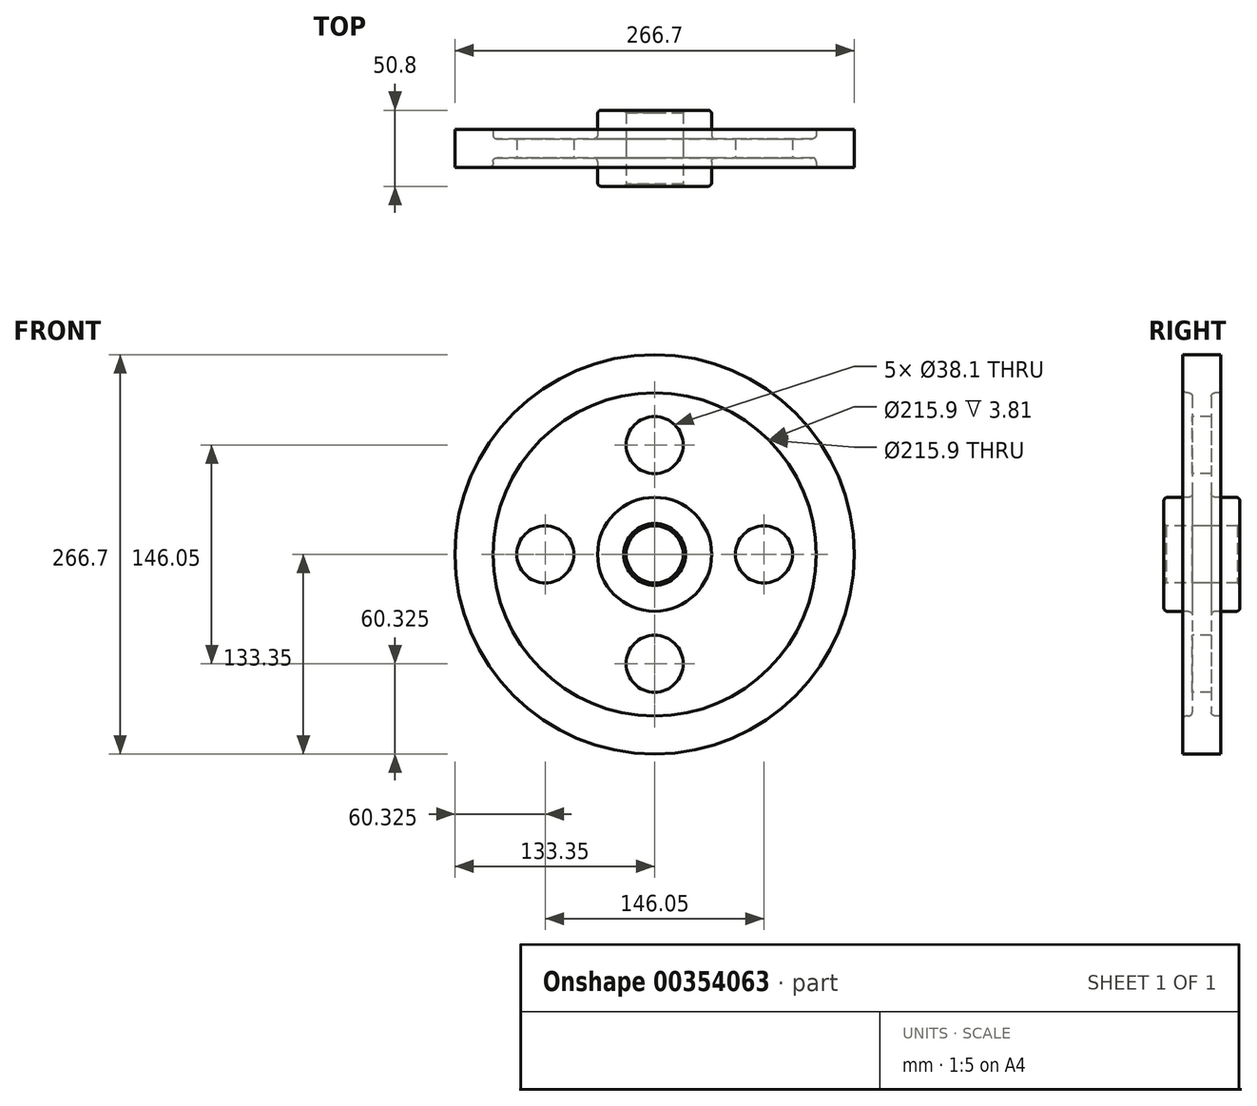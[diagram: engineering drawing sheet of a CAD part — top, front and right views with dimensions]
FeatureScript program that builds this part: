
annotation { "Feature Type Name" : "Feature", "Feature Type Description" : "" }
export const myFeature = defineFeature(function(context is Context, id is Id, definition is map)
    precondition{}
    {
        {
            var Q0;
            Q0=qCreatedBy(makeId("Right.planeOp"),FACE);
            var sketch = newSketch(context, id + "F0", { "sketchPlane" : qUnion([Q0])});
            skLineSegment(sketch, "E0", {"start": v(0, 0) * mm, "end": v(94.54, 0) * mm, "construction": true});
            skLineSegment(sketch, "E1.0", {"start": v(0, 19.05) * mm, "end": v(25.4, 19.05) * mm});
            skLineSegment(sketch, "E2.0", {"start": v(6.35, 38.1) * mm, "end": v(25.4, 38.1) * mm});
            skLineSegment(sketch, "E3.0", {"start": v(6.35, 107.95) * mm, "end": v(12.7, 107.95) * mm});
            skLineSegment(sketch, "E4.0", {"start": v(0, 133.35) * mm, "end": v(12.7, 133.35) * mm});
            skLineSegment(sketch, "E5", {"start": v(0, 133.35) * mm, "end": v(0, 0) * mm, "construction": true});
            skLineSegment(sketch, "E6.0", {"start": v(25.4, 38.1) * mm, "end": v(25.4, 19.05) * mm});
            skLineSegment(sketch, "E7.0", {"start": v(6.35, 107.95) * mm, "end": v(6.35, 38.1) * mm});
            skLineSegment(sketch, "E8.0", {"start": v(12.7, 133.35) * mm, "end": v(12.7, 107.95) * mm});
            skLineSegment(sketch, "E9.MirrorCS", {"start": v(0, 133.35) * mm, "end": v(-12.7, 133.35) * mm});
            skLineSegment(sketch, "E10.MirrorCS", {"start": v(-12.7, 133.35) * mm, "end": v(-12.7, 107.95) * mm});
            skLineSegment(sketch, "E11.MirrorCS", {"start": v(-6.35, 107.95) * mm, "end": v(-6.35, 38.1) * mm});
            skLineSegment(sketch, "E12.MirrorCS", {"start": v(-6.35, 38.1) * mm, "end": v(-25.4, 38.1) * mm});
            skLineSegment(sketch, "E13.MirrorCS", {"start": v(-25.4, 38.1) * mm, "end": v(-25.4, 19.05) * mm});
            skLineSegment(sketch, "E14.MirrorCS", {"start": v(0, 19.05) * mm, "end": v(-25.4, 19.05) * mm});
            skLineSegment(sketch, "E15", {"start": v(-12.7, 107.95) * mm, "end": v(-6.35, 107.95) * mm});
            skSolve(sketch);
        }
        {
            var Q0;
            Q0=makeQuery(id+"F0.imprint","IMPRINT",FACE,{"disambiguationData":[TD([[makeQuery(id+"F0.imprint","IMPRINT",EDGE,{"derivedFrom":sQuery(id+"F0.wireOp",EDGE,"E1.0")}),1.0]])]});
            var Q1;
            Q1=sQuery(id+"F0.wireOp",EDGE,"E0");
            revolve(context, id + "F1", {"entities" : qUnion([Q0]), "axis" : qUnion([Q1]), "revolveType" : RevolveType.FULL});
        }
        {
            var Q0;
            Q0=makeQuery(id+"F1.opRevolve","SWEPT_FACE",FACE,{"disambiguationData":[OSD([sQuery(id+"F0.wireOp",EDGE,"E11.MirrorCS")])]});
            var sketch = newSketch(context, id + "F2", { "sketchPlane" : qUnion([Q0])});
            skLineSegment(sketch, "E16", {"start": v(0, 0) * mm, "end": v(0, 73.03) * mm});
            skCircle(sketch, "E17", {"center": v(0, 73.03) * mm, "radius": 19.05 * mm});
            skPoint(sketch, "E18.center", {"position": v(0, 0) * mm});
            skCircle(sketch, "E19.1.0", {"center": v(-73.03, 0) * mm, "radius": 19.05 * mm});
            skCircle(sketch, "E19.2.0", {"center": v(0, -73.03) * mm, "radius": 19.05 * mm});
            skCircle(sketch, "E19.3.0", {"center": v(73.03, 0) * mm, "radius": 19.05 * mm});
            skSolve(sketch);
        }
        {
            var Q0;
            Q0=makeQuery(id+"F2.imprint","IMPRINT",FACE,{"disambiguationData":[TD([[makeQuery(id+"F2.imprint","IMPRINT",EDGE,{"derivedFrom":sQuery(id+"F2.wireOp",EDGE,"E17")}),1.0]])]});
            var Q1;
            Q1=makeQuery(id+"F2.imprint","IMPRINT",FACE,{"disambiguationData":[TD([[makeQuery(id+"F2.imprint","IMPRINT",EDGE,{"derivedFrom":sQuery(id+"F2.wireOp",EDGE,"E19.3.0")}),1.0]])]});
            var Q2;
            Q2=makeQuery(id+"F2.imprint","IMPRINT",FACE,{"disambiguationData":[TD([[makeQuery(id+"F2.imprint","IMPRINT",EDGE,{"derivedFrom":sQuery(id+"F2.wireOp",EDGE,"E19.2.0")}),1.0]])]});
            var Q3;
            Q3=makeQuery(id+"F2.imprint","IMPRINT",FACE,{"disambiguationData":[TD([[makeQuery(id+"F2.imprint","IMPRINT",EDGE,{"derivedFrom":sQuery(id+"F2.wireOp",EDGE,"E19.1.0")}),1.0]])]});
            extrude(context, id + "F3", {"entities" : qUnion([Q0, Q1, Q2, Q3]), "operationType" : NewBodyOperationType.REMOVE, "oppositeDirection" : true, "depth" : 25.4 * mm});
        }
        {
            var Q0;
            Q0=makeQuery(id+"F1.opRevolve","SWEPT_EDGE",EDGE,{"disambiguationData":[OSD([sQuery(id+"F0.wireOp",EDGE,"E12.MirrorCS"),sQuery(id+"F0.wireOp",EDGE,"E13.MirrorCS")])]});
            var Q1;
            Q1=makeQuery(id+"F1.opRevolve","SWEPT_EDGE",EDGE,{"disambiguationData":[OSD([sQuery(id+"F0.wireOp",EDGE,"E11.MirrorCS"),sQuery(id+"F0.wireOp",EDGE,"E12.MirrorCS")])]});
            var Q2;
            Q2=makeQuery(id+"F1.opRevolve","SWEPT_EDGE",EDGE,{"disambiguationData":[OSD([sQuery(id+"F0.wireOp",EDGE,"E11.MirrorCS"),sQuery(id+"F0.wireOp",EDGE,"E15")])]});
            var Q3;
            Q3=makeQuery(id+"F1.opRevolve","SWEPT_EDGE",EDGE,{"disambiguationData":[OSD([sQuery(id+"F0.wireOp",EDGE,"E10.MirrorCS"),sQuery(id+"F0.wireOp",EDGE,"E15")])]});
            var Q4;
            Q4=makeQuery(id+"F1.opRevolve","SWEPT_EDGE",EDGE,{"disambiguationData":[OSD([sQuery(id+"F0.wireOp",EDGE,"E2.0"),sQuery(id+"F0.wireOp",EDGE,"E7.0")])]});
            var Q5;
            Q5=makeQuery(id+"F1.opRevolve","SWEPT_EDGE",EDGE,{"disambiguationData":[OSD([sQuery(id+"F0.wireOp",EDGE,"E7.0"),sQuery(id+"F0.wireOp",EDGE,"E3.0")])]});
            var Q6;
            Q6=makeQuery(id+"F1.opRevolve","SWEPT_EDGE",EDGE,{"disambiguationData":[OSD([sQuery(id+"F0.wireOp",EDGE,"E2.0"),sQuery(id+"F0.wireOp",EDGE,"E6.0")])]});
            fillet(context, id + "F4", {"entities" : qUnion([Q0, Q1, Q2, Q3, Q4, Q5, Q6]), "radius" : 2.54 * mm, "tangentPropagation" : true, "allowEdgeOverflow" : false});
        }
        {
            var Q0;
            Q0=makeQuery(id+"F1.opRevolve","SWEPT_EDGE",EDGE,{"disambiguationData":[OSD([sQuery(id+"F0.wireOp",EDGE,"E13.MirrorCS"),sQuery(id+"F0.wireOp",EDGE,"E14.MirrorCS")])]});
            var Q1;
            Q1=makeQuery(id+"F1.opRevolve","SWEPT_EDGE",EDGE,{"disambiguationData":[OSD([sQuery(id+"F0.wireOp",EDGE,"E1.0"),sQuery(id+"F0.wireOp",EDGE,"E6.0")])]});
            chamfer(context, id + "F5", {"entities" : qUnion([Q0, Q1]), "width" : 1.59 * mm, "tangentPropagation" : true});
        }
    });
